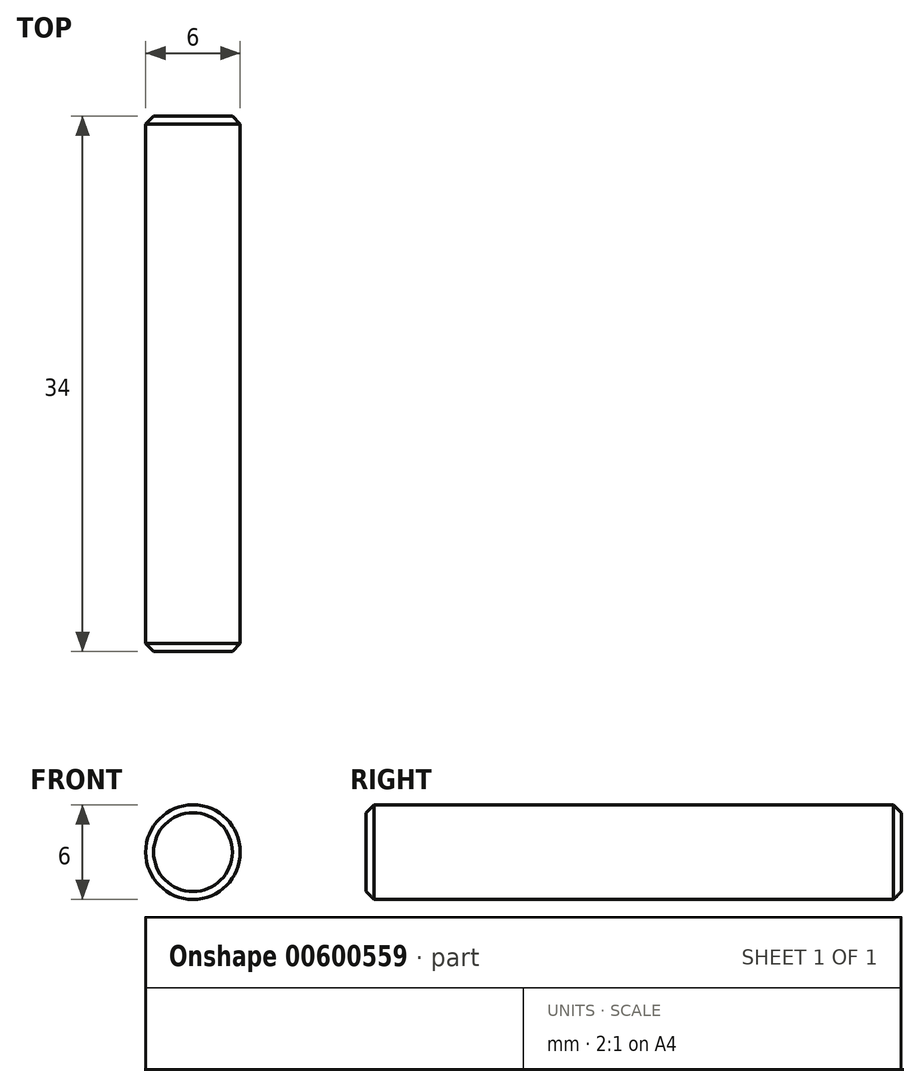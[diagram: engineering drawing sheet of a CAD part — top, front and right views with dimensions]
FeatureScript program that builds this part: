
annotation { "Feature Type Name" : "Feature", "Feature Type Description" : "" }
export const myFeature = defineFeature(function(context is Context, id is Id, definition is map)
    precondition{}
    {
        {
            var Q0;
            Q0=qCreatedBy(makeId("Front.planeOp"),FACE);
            var sketch = newSketch(context, id + "F0", { "sketchPlane" : qUnion([Q0])});
            skCircle(sketch, "E0", {"center": v(0, 0) * mm, "radius": 3 * mm});
            skSolve(sketch);
        }
        {
            var Q0;
            Q0 = qSketchRegion(id + "F0", true);
            extrude(context, id + "F1", {"entities" : qUnion([Q0]), "oppositeDirection" : true, "depth" : 34 * mm, "offsetDistance" : 25 * mm});
        }
        {
            var Q0;
            Q0=makeQuery(id+"F1.opExtrude","CAP_EDGE",EDGE,{"disambiguationData":[OSD([sQuery(id+"F0.wireOp",EDGE,"E0")])],"isStart":true});
            var Q1;
            Q1=makeQuery(id+"F1.opExtrude","CAP_EDGE",EDGE,{"disambiguationData":[OSD([sQuery(id+"F0.wireOp",EDGE,"E0")])],"isStart":false});
            chamfer(context, id + "F2", {"entities" : qUnion([Q0, Q1]), "width" : 0.5 * mm, "tangentPropagation" : true});
        }
    });
